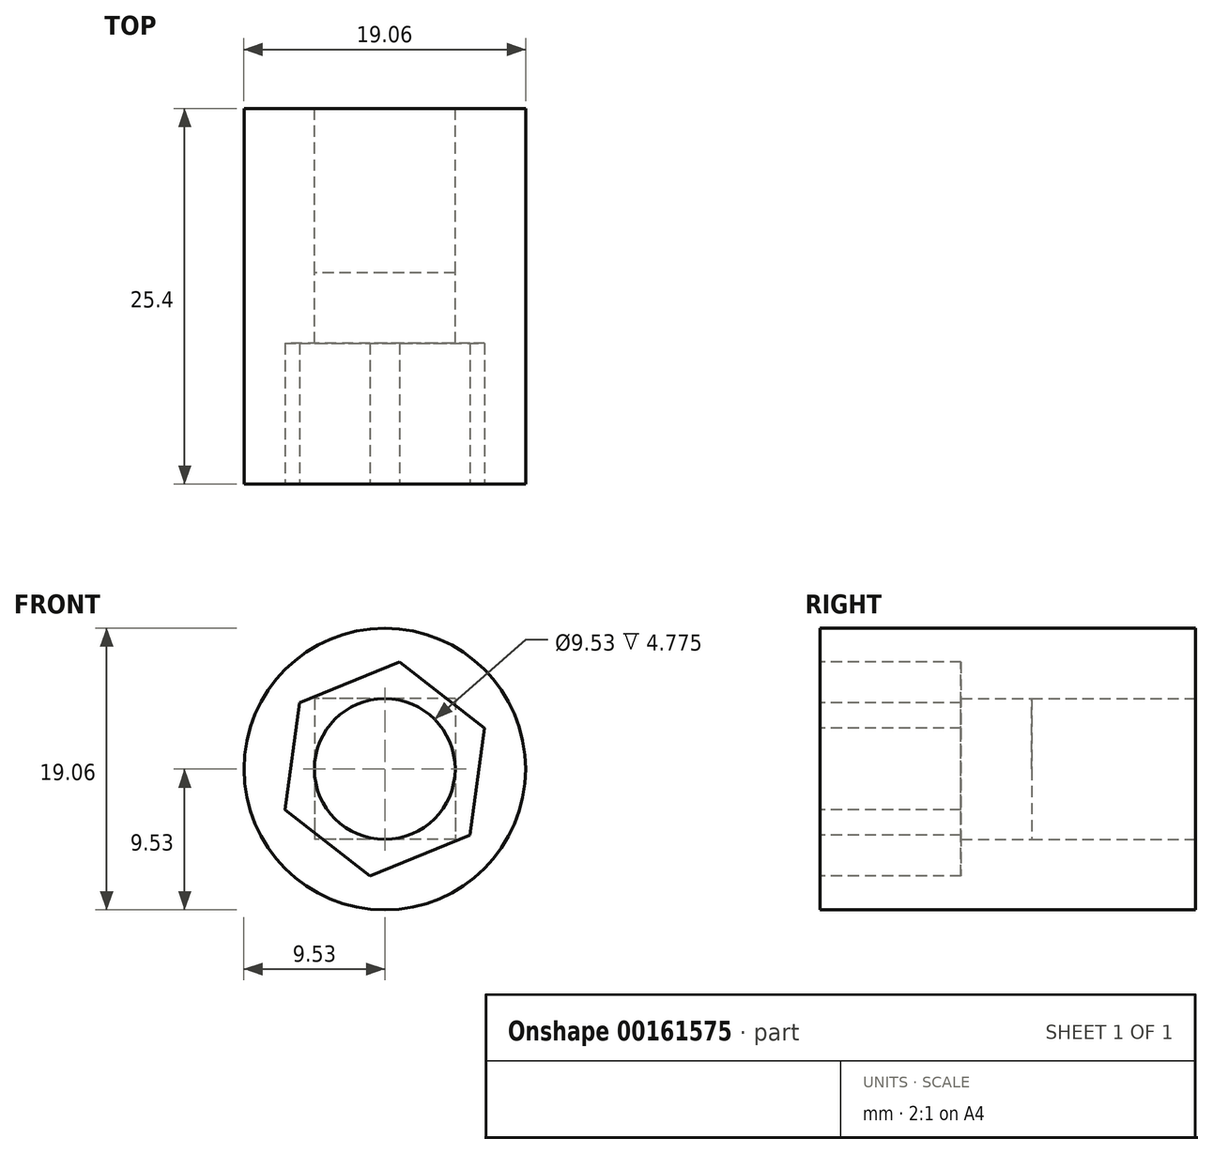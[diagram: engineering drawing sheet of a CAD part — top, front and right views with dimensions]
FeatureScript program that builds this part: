
annotation { "Feature Type Name" : "Feature", "Feature Type Description" : "" }
export const myFeature = defineFeature(function(context is Context, id is Id, definition is map)
    precondition{}
    {
        {
            var Q0;
            Q0=qCreatedBy(makeId("Front.planeOp"),FACE);
            var sketch = newSketch(context, id + "F0", { "sketchPlane" : qUnion([Q0])});
            skCircle(sketch, "E0", {"center": v(0, 0) * mm, "radius": 9.53 * mm});
            skSolve(sketch);
        }
        {
            var Q0;
            Q0=makeQuery(id+"F0.imprint","IMPRINT",FACE,{"disambiguationData":[TD([[makeQuery(id+"F0.imprint","IMPRINT",EDGE,{"derivedFrom":sQuery(id+"F0.wireOp",EDGE,"E0")}),1.0]])]});
            extrude(context, id + "F1", {"entities" : qUnion([Q0]), "depth" : 25.4 * mm});
        }
        {
            var Q0;
            Q0=qCreatedBy(makeId("Front.planeOp"),FACE);
            var sketch = newSketch(context, id + "F2", { "sketchPlane" : qUnion([Q0])});
            skLineSegment(sketch, "E1.bottom", {"start": v(4.76, 4.76) * mm, "end": v(-4.76, 4.76) * mm});
            skLineSegment(sketch, "E1.top", {"start": v(4.76, -4.76) * mm, "end": v(-4.76, -4.76) * mm});
            skLineSegment(sketch, "E1.left", {"start": v(4.76, 4.76) * mm, "end": v(4.76, -4.76) * mm});
            skLineSegment(sketch, "E1.right", {"start": v(-4.76, 4.76) * mm, "end": v(-4.76, -4.76) * mm});
            skPoint(sketch, "E1.middle", {"position": v(0, 0) * mm});
            skCircle(sketch, "E2", {"center": v(0, 0) * mm, "radius": 4.76 * mm});
            skSolve(sketch);
        }
        {
            var Q0;
            {var subQ0=sQuery(id+"F2.wireOp",EDGE,"E2");var subQ1=makeQuery(id+"F2.imprint","INTERSECT",VERTEX,{"derivedFrom":[sQuery(id+"F2.wireOp",EDGE,"E1.bottom"),subQ0]});Q0=makeQuery(id+"F2.imprint","IMPRINT",FACE,{"disambiguationData":[TD([[makeQuery(id+"F2.imprint","IMPRINT",EDGE,{"disambiguationData":[TD([[subQ1,1.0]])],"derivedFrom":subQ0}),1.0]])]});}
            extrude(context, id + "F3", {"entities" : qUnion([Q0]), "operationType" : NewBodyOperationType.REMOVE, "endBound" : BoundingType.THROUGH_ALL, "depth" : 25.4 * mm});
        }
        {
            var Q0;
            Q0 = qSketchRegion(id + "F2", true);
            extrude(context, id + "F4", {"entities" : qUnion([Q0]), "operationType" : NewBodyOperationType.REMOVE, "depth" : 11.1 * mm});
        }
        {
            var Q0;
            Q0=makeQuery(id+"F1.opExtrude","CAP_FACE",FACE,{"disambiguationData":[OSD([sQuery(id+"F0.wireOp",EDGE,"E0")])],"isStart":false});
            var sketch = newSketch(context, id + "F5", { "sketchPlane" : qUnion([Q0])});
            skCircle(sketch, "E3.cCircle", {"center": v(0, 0) * mm, "radius": 6.32 * mm, "construction": true});
            skLineSegment(sketch, "E3.0", {"start": v(-5.77, 4.48) * mm, "end": v(1, 7.23) * mm});
            skLineSegment(sketch, "E3.1", {"start": v(1, 7.23) * mm, "end": v(6.76, 2.76) * mm});
            skLineSegment(sketch, "E3.2", {"start": v(6.76, 2.76) * mm, "end": v(5.77, -4.48) * mm});
            skLineSegment(sketch, "E3.3", {"start": v(5.77, -4.48) * mm, "end": v(-1, -7.23) * mm});
            skLineSegment(sketch, "E3.4", {"start": v(-1, -7.23) * mm, "end": v(-6.76, -2.76) * mm});
            skLineSegment(sketch, "E3.5", {"start": v(-6.76, -2.76) * mm, "end": v(-5.77, 4.48) * mm});
            skPoint(sketch, "E3.0.midPoint", {"position": v(-2.39, 5.86) * mm});
            skSolve(sketch);
        }
        {
            var Q0;
            Q0 = qSketchRegion(id + "F5", true);
            extrude(context, id + "F6", {"entities" : qUnion([Q0]), "operationType" : NewBodyOperationType.REMOVE, "oppositeDirection" : true, "depth" : 9.52 * mm});
        }
    });
